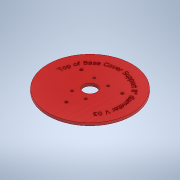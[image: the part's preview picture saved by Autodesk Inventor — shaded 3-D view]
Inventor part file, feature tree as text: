
AUTODESK INVENTOR PART (.ipt)
format: ipt  version: 2022.2 (Build 262287010, 287A)  size: 1,077,760 bytes
history: native  units: in
note: dims shown in document units (in); Inventor stores cm internally (conversion verified against a paired STEP export)
features: sketch x6, extrude x4, hole x2, emboss x1, projected_geometry x1
ambient origin geometry x8: Origin, YZ Plane, XZ Plane, XY Plane, X Axis, Y Axis, Z Axis, Center Point
bodies: Solid1 (feature_tree)
feature tree (14):
  extrude  "Extrusion1"  Depth=0.25in TaperAngle=0.0deg
  extrude  "Extrusion4"  Depth=1.5in
  extrude  "Extrusion7"  Depth=0.25in
  hole  "Hole2"  [1 undecoded]
  hole  "Hole3"  [1 undecoded]
  extrude  "Extrusion8"  Depth=0.1in
  emboss  "Emboss1"
  sketch  "Sketch3"  dims[d0=4.25in d1=0.25in d2=0.0in]
  sketch  "Sketch5"  dims[d6=2.75in d7=1.5in]
  sketch  "Sketch9"  dims[d8=0.25in d9=0.25in]
  sketch  "Sketch10"  dims[d10=0.25in d11=0.25in]
  sketch  "Sketch11"  dims[d14=0.25in d15=0.0in d24=1.25in]
  projected_geometry  "Projected Loop1"
  sketch  "Sketch13"  dims[d25=0.0in d26=0.0in d42=0.875in d43=1.75in d44=2.5in d45=0.1875in d46=0.228in d47=0.75in d48=0.563in d49=0.155in d50=0.5635in d51=0.125in d52=0.0in d53=2.125in d54=1.317in d55=4.5in d56=1.1811in d58=360.0deg d60=0.15in d61=0.75in d62=0.27in d63=0.08in d64=0.5635in d65=1.0in d66=0.8108in d67=8.0in d68=0.25in d69=0.0in d70=6.0in d71=0.1in d72=0.0in]
note: 2 required parameter values undecoded (feature->parameter linkage not recoverable at this tier; creation-order binding heuristic only, values carry confidence <= 0.55)
